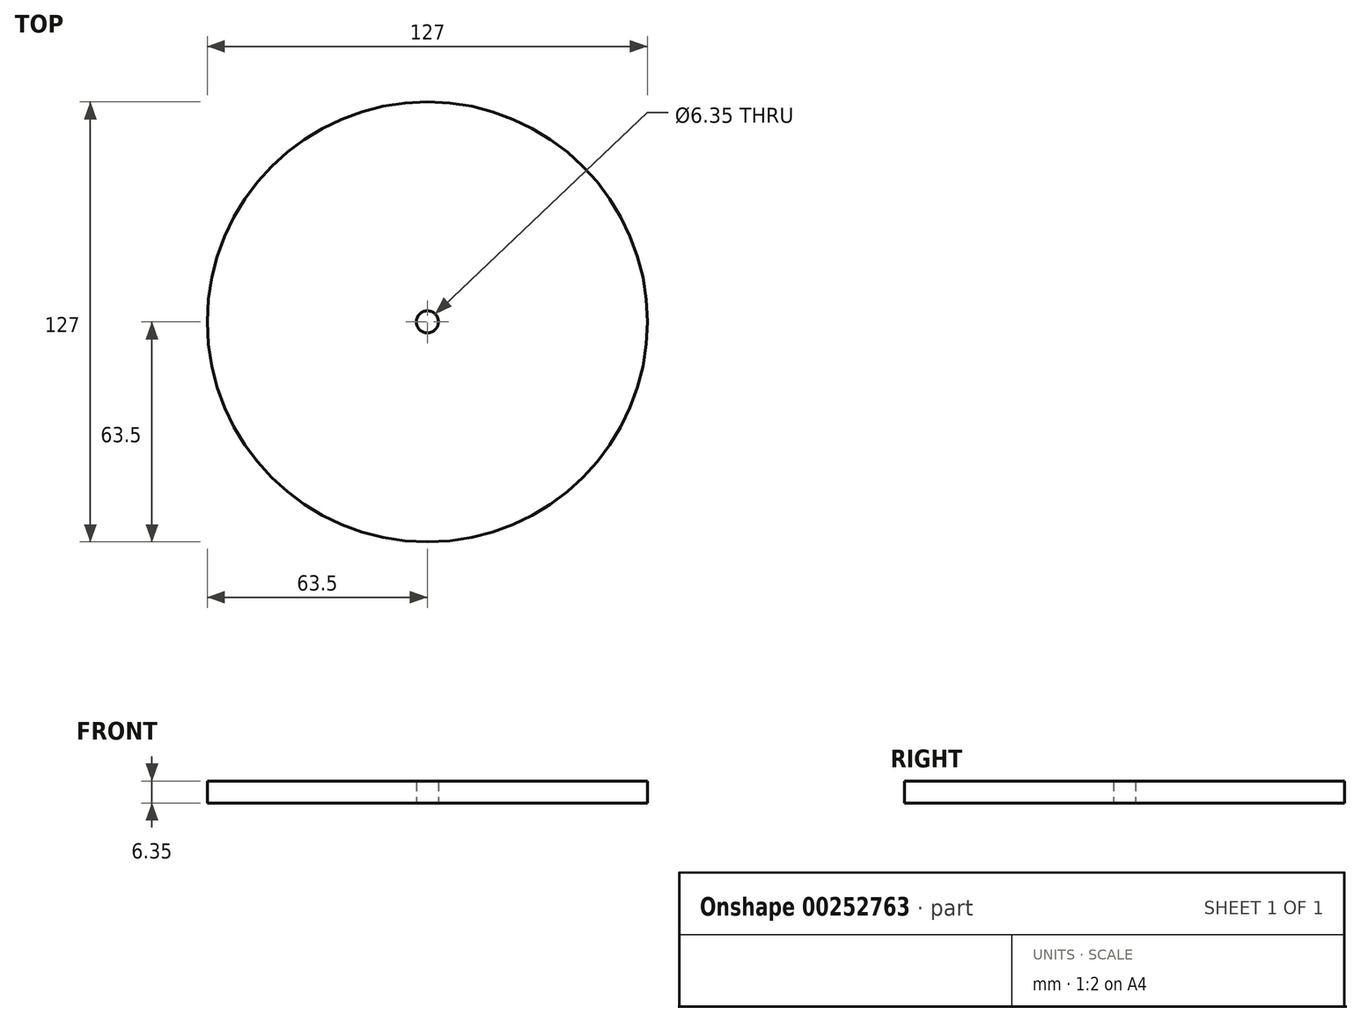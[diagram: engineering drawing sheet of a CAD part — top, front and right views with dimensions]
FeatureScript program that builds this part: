
annotation { "Feature Type Name" : "Feature", "Feature Type Description" : "" }
export const myFeature = defineFeature(function(context is Context, id is Id, definition is map)
    precondition{}
    {
        {
            var Q0;
            Q0=qCreatedBy(makeId("Top.planeOp"),FACE);
            var sketch = newSketch(context, id + "F0", { "sketchPlane" : qUnion([Q0])});
            skCircle(sketch, "E0", {"center": v(0, 0) * mm, "radius": 63.5 * mm});
            skCircle(sketch, "E1", {"center": v(0, 0) * mm, "radius": 3.18 * mm});
            skSolve(sketch);
        }
        {
            var Q0;
            Q0=makeQuery(id+"F0.imprint","IMPRINT",FACE,{"disambiguationData":[TD([[makeQuery(id+"F0.imprint","IMPRINT",EDGE,{"derivedFrom":sQuery(id+"F0.wireOp",EDGE,"E0")}),1.0]])]});
            extrude(context, id + "F1", {"entities" : qUnion([Q0]), "depth" : 6.35 * mm});
        }
    });
